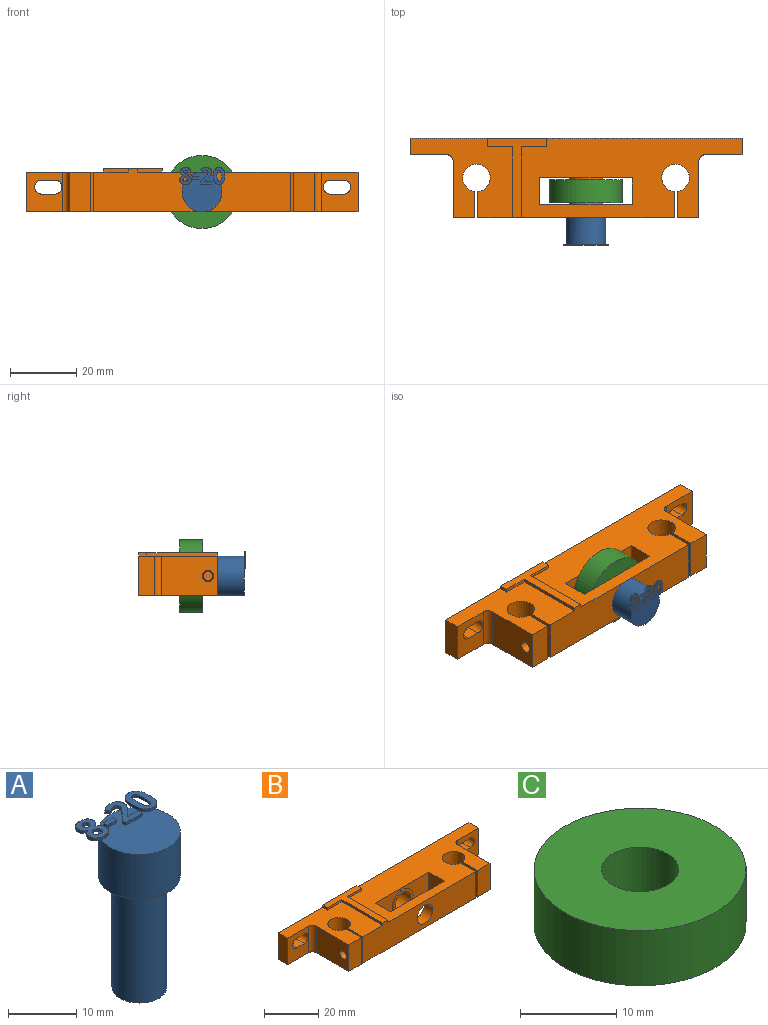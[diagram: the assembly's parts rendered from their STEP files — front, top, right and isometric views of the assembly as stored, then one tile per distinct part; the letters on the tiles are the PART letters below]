
ASSEMBLY  parts=3 mates=2
PART A: 89 faces, bbox 13.6x13.4x28.5 mm
  f0: plane 0.75x0.57mm, normal (0,0,1), area 0.1mm2, adj f5,f78,f79
  f1: plane 12x12mm, normal (0,0,1), area 100.3mm2, adj f5,f22,f23,f24,f25,f26,f40,f41
  f2: plane 1.04x0.97mm, normal (0,0,1), area 0.5mm2, adj f5,f29,f30,f31,f32,f33
  f3: cylinder r=4mm len=20mm, axis (0,0,-1), area 502.7mm2, adj f4,f6
  f4: plane 8x8mm, normal (0,0,-1), area 50.3mm2, adj f3
  f5: cylinder r=6mm len=12mm, axis (0,0,-1), area 301.6mm2, adj f0,f1,f2,f6,f39,f70,f88
  f6: plane 12x12mm, normal (0,0,-1), area 62.8mm2, adj f3,f5
  f7: extruded ~0.5x0.43mm, area 0.2mm2, adj f8,f37,f38,f39
  f8: extruded ~0.5x0.43mm, area 0.2mm2, adj f7,f9,f38,f39
  f9: extruded ~0.5x0.37mm, area 0.2mm2, adj f8,f10,f38,f39
  f10: extruded ~0.5x0.38mm, area 0.2mm2, adj f9,f11,f38,f39
  f11: extruded ~0.5x0.46mm, area 0.3mm2, adj f10,f12,f38,f39
  f12: extruded ~0.5x0.47mm, area 0.3mm2, adj f11,f13,f38,f39
  f13: extruded ~0.5x0.36mm, area 0.2mm2, adj f12,f37,f38,f39
  f14: extruded ~1.15x0.5mm, area 0.6mm2, adj f15,f35,f38,f39
  f15: extruded ~1.15x0.5mm, area 0.6mm2, adj f14,f16,f38,f39
  f16: extruded ~0.86x0.5mm, area 0.5mm2, adj f15,f17,f38,f39
  f17: extruded ~0.67x0.5mm, area 0.4mm2, adj f16,f18,f38,f39
  f18: extruded ~0.61x0.57mm, area 0.4mm2, adj f17,f19,f38,f39
  f19: extruded ~0.72x0.58mm, area 0.5mm2, adj f18,f20,f38,f39
  f20: extruded ~0.75x0.5mm, area 0.4mm2, adj f19,f21,f38,f39
  f21: extruded ~0.98x0.5mm, area 0.6mm2, adj f20,f22,f38,f39
  f22: extruded ~1.28x0.5mm, area 0.7mm2, adj f1,f21,f23,f38,f39
  f23: extruded ~1.26x0.5mm, area 0.7mm2, adj f1,f22,f24,f38
  f24: extruded ~0.98x0.5mm, area 0.6mm2, adj f1,f23,f25,f38
  f25: extruded ~0.71x0.5mm, area 0.4mm2, adj f1,f24,f26,f38
  f26: extruded ~0.8x0.62mm, area 0.5mm2, adj f1,f25,f27,f38,f39
  f27: extruded ~0.68x0.53mm, area 0.4mm2, adj f26,f28,f38,f39
  f28: extruded ~0.68x0.5mm, area 0.4mm2, adj f27,f35,f38,f39
  f29: extruded ~0.62x0.5mm, area 0.4mm2, adj f2,f30,f36,f38,f39
  f30: extruded ~0.5x0.43mm, area 0.2mm2, adj f2,f29,f31,f38
  f31: extruded ~0.5x0.44mm, area 0.2mm2, adj f2,f30,f32,f38
  f32: extruded ~0.58x0.5mm, area 0.3mm2, adj f2,f31,f33,f38
  f33: extruded ~0.56x0.5mm, area 0.3mm2, adj f2,f32,f34,f38,f39
  f34: extruded ~0.5x0.45mm, area 0.3mm2, adj f33,f36,f38,f39
  f35: extruded ~0.87x0.5mm, area 0.5mm2, adj f14,f28,f38,f39
  f36: extruded ~0.84x0.72mm, area 0.6mm2, adj f29,f34,f38,f39
  f37: extruded ~0.5x0.37mm, area 0.2mm2, adj f7,f13,f38,f39
  f38: plane 5.09x3.48mm, normal (0,0,1), area 11.2mm2, adj f7,f8,f9,f10,f11,f12,f13,f14
  f39: plane 5.05x3.32mm, normal (0,0,-1), area 8.6mm2, adj f5,f7,f8,f9,f10,f11,f12,f13
  f40: plane 0.85x0.5mm, normal (-1,0,0), area 0.4mm2, adj f1,f41,f43,f44
  f41: plane 1.82x0.5mm, normal (0,-1,0), area 0.9mm2, adj f1,f40,f42,f44
  f42: plane 0.85x0.5mm, normal (1,0,0), area 0.4mm2, adj f1,f41,f43,f44
  f43: plane 1.82x0.5mm, normal (0,1,0), area 0.9mm2, adj f1,f40,f42,f44
  f44: plane 1.82x0.85mm, normal (0,0,1), area 1.5mm2, adj f40,f41,f42,f43
  f45: extruded ~0.5x0.39mm, area 0.2mm2, adj f1,f46,f68,f69,f70
  f46: extruded ~0.5x0.41mm, area 0.2mm2, adj f1,f45,f47,f69
  f47: extruded ~0.78x0.72mm, area 0.5mm2, adj f1,f46,f48,f69
  f48: plane 1.26x1.24mm, normal (-0.71,0.7,0), area 0.9mm2, adj f1,f47,f49,f69
  f49: plane 0.73x0.5mm, normal (-1,0,0), area 0.4mm2, adj f1,f48,f50,f69
  f50: plane 3.46x0.5mm, normal (0,-1,0), area 1.7mm2, adj f1,f49,f51,f69
  f51: plane 0.88x0.5mm, normal (1,0,0), area 0.4mm2, adj f1,f50,f52,f69
  f52: plane 2.16x0.5mm, normal (0,1,0), area 1.1mm2, adj f1,f51,f53,f69
  f53: plane 0.5x0.05mm, normal (1,0,0), area 0mm2, adj f1,f52,f54,f69
  f54: plane 0.64x0.6mm, normal (0.69,-0.73,0), area 0.4mm2, adj f1,f53,f55,f69
  f55: extruded ~0.9x0.89mm, area 0.6mm2, adj f1,f54,f56,f69
  f56: extruded ~0.62x0.5mm, area 0.4mm2, adj f1,f55,f57,f69,f70
  f57: extruded ~0.64x0.5mm, area 0.3mm2, adj f56,f58,f69,f70
  f58: extruded ~0.7x0.5mm, area 0.4mm2, adj f57,f59,f69,f70
  f59: extruded ~0.55x0.5mm, area 0.4mm2, adj f58,f60,f69,f70
  f60: extruded ~0.82x0.5mm, area 0.4mm2, adj f59,f61,f69,f70
  f61: extruded ~0.64x0.5mm, area 0.3mm2, adj f60,f62,f69,f70
  f62: extruded ~0.53x0.5mm, area 0.3mm2, adj f61,f63,f69,f70
  f63: extruded ~0.61x0.5mm, area 0.4mm2, adj f62,f64,f69,f70
  f64: plane 0.67x0.57mm, normal (-0.76,-0.65,0), area 0.4mm2, adj f63,f65,f69,f70
  f65: extruded ~0.57x0.5mm, area 0.3mm2, adj f64,f66,f69,f70
  f66: extruded ~0.56x0.5mm, area 0.3mm2, adj f65,f67,f69,f70
  f67: extruded ~0.5x0.44mm, area 0.2mm2, adj f66,f68,f69,f70
  f68: extruded ~0.5x0.44mm, area 0.2mm2, adj f45,f67,f69,f70
  f69: plane 5.03x3.48mm, normal (0,0,1), area 9.1mm2, adj f45,f46,f47,f48,f49,f50,f51,f52
  f70: plane 3.34x2.04mm, normal (0,0,-1), area 3.5mm2, adj f5,f45,f56,f57,f58,f59,f60,f61
  f71: extruded ~1.92x0.5mm, area 1mm2, adj f72,f86,f87,f88
  f72: extruded ~1.91x0.5mm, area 1mm2, adj f71,f73,f87,f88
  f73: extruded ~1.3x0.65mm, area 0.8mm2, adj f72,f74,f87,f88
  f74: extruded ~1.3x0.62mm, area 0.8mm2, adj f73,f75,f87,f88
  f75: extruded ~1.93x0.5mm, area 1mm2, adj f1,f74,f76,f87,f88
  f76: extruded ~1.9x0.5mm, area 1mm2, adj f1,f75,f77,f87
  f77: extruded ~1.29x0.64mm, area 0.8mm2, adj f1,f76,f86,f87
  f78: extruded ~0.53x0.5mm, area 0.4mm2, adj f0,f79,f85,f87,f88
  f79: extruded ~1.31x0.5mm, area 0.7mm2, adj f0,f78,f80,f87,f88
  f80: extruded ~1.31x0.5mm, area 0.7mm2, adj f79,f81,f87,f88
  f81: extruded ~0.53x0.5mm, area 0.4mm2, adj f80,f82,f87,f88
  f82: extruded ~0.53x0.5mm, area 0.4mm2, adj f81,f83,f87,f88
  f83: extruded ~1.31x0.5mm, area 0.7mm2, adj f82,f84,f87,f88
  f84: extruded ~1.3x0.5mm, area 0.7mm2, adj f83,f85,f87,f88
  f85: extruded ~0.53x0.5mm, area 0.4mm2, adj f78,f84,f87,f88
  f86: extruded ~1.31x0.62mm, area 0.8mm2, adj f1,f71,f77,f87,f88
  f87: plane 5.1x3.46mm, normal (0,0,1), area 10.7mm2, adj f71,f72,f73,f74,f75,f76,f77,f78
  f88: plane 5.1x3.46mm, normal (0,0,-1), area 8.4mm2, adj f5,f71,f72,f73,f74,f75,f78,f79
PART B: 53 faces, bbox 100x24x13 mm
  f0: plane 100x24mm, normal (0,0,1), area 1458.9mm2, adj f2,f3,f4,f5,f6,f7,f8,f9
  f1: plane 100x24mm, normal (0,0,-1), area 1561.7mm2, adj f2,f3,f4,f5,f6,f7,f8,f9
  f2: plane 100x12mm, normal (0,1,0), area 1138.7mm2, adj f0,f1,f6,f11,f18,f19,f20,f21
  f3: plane 12x11mm, normal (0,-1,0), area 101.3mm2, adj f0,f1,f11,f22,f23,f24,f25,f48
  f4: plane 12x6.56mm, normal (0,-1,0), area 78.7mm2, adj f0,f1,f10,f16
  f5: plane 59.12x13mm, normal (0,-1,0), area 659.4mm2, adj f0,f1,f14,f17,f26,f37,f38,f44
  f6: plane 12x5mm, normal (-1,0,0), area 60mm2, adj f0,f1,f2,f7
  f7: plane 12x11mm, normal (0,-1,0), area 101.3mm2, adj f0,f1,f6,f18,f19,f20,f21,f52
  f8: plane 17x12mm, normal (-1,0,0), area 194.9mm2, adj f0,f1,f9,f51,f52
  f9: plane 12x6.56mm, normal (0,-1,0), area 78.7mm2, adj f0,f1,f8,f13
  f10: plane 17x12mm, normal (1,0,0), area 194.9mm2, adj f0,f1,f4,f47,f48
  f11: plane 12x5mm, normal (1,0,0), area 60mm2, adj f0,f1,f2,f3
  f12: cylinder r=4.15mm len=12mm, axis (0,0,1), area 302.4mm2, adj f0,f1,f13,f14
  f13: plane 12x7.87mm, normal (1,0,0), area 85.4mm2, adj f0,f1,f9,f12,f51
  f14: plane 12x7.87mm, normal (-1,0,0), area 88.3mm2, adj f0,f1,f5,f12,f50
  f15: cylinder r=4.15mm len=12mm, axis (0,0,1), area 302.4mm2, adj f0,f1,f16,f17
  f16: plane 12x7.87mm, normal (-1,0,0), area 85.4mm2, adj f0,f1,f4,f15,f47
  f17: plane 12x7.87mm, normal (1,0,0), area 88.3mm2, adj f0,f1,f5,f15,f46
  f18: cylinder r=2.1mm len=5mm, axis (0,1,0), area 33mm2, adj f2,f7,f19,f21
  f19: plane 5x4mm, normal (0,0,1), area 20mm2, adj f2,f7,f18,f20
  f20: cylinder r=2.1mm len=5mm, axis (0,1,0), area 33mm2, adj f2,f7,f19,f21
  f21: plane 5x4mm, normal (0,0,-1), area 20mm2, adj f2,f7,f18,f20
  f22: plane 5x4mm, normal (0,0,-1), area 20mm2, adj f2,f3,f23,f25
  f23: cylinder r=2.1mm len=5mm, axis (0,1,0), area 33mm2, adj f2,f3,f22,f24
  f24: plane 5x4mm, normal (0,0,1), area 20mm2, adj f2,f3,f23,f25
  f25: cylinder r=2.1mm len=5mm, axis (0,1,0), area 33mm2, adj f2,f3,f22,f24
  f26: cylinder r=4.1mm len=8.2mm, axis (0,-1,0), area 115.9mm2, adj f5,f36
  f27: plane 12x8mm, normal (1,0,0), area 96mm2, adj f0,f1,f29,f30
  f28: plane 12x8mm, normal (-1,0,0), area 96mm2, adj f0,f1,f29,f30
  f29: plane 28x12mm, normal (0,-1,0), area 251.2mm2, adj f0,f1,f27,f28,f31
  f30: plane 28x12mm, normal (0,1,0), area 249.3mm2, adj f0,f1,f27,f28,f35
  f31: cylinder r=5.2mm len=10.39mm, axis (0,1,0), area 16.3mm2, adj f29,f32
  f32: plane 10.39x10.39mm, normal (0,-1,0), area 32mm2, adj f31,f34
  f33: plane 8.2x8.2mm, normal (0,-1,0), area 52.8mm2, adj f34
  f34: cylinder r=4.1mm len=8.5mm, axis (0,-1,0), area 219mm2, adj f32,f33
  f35: cylinder r=5.25mm len=10.51mm, axis (0,-1,0), area 16.5mm2, adj f30,f36
  f36: plane 10.51x10.51mm, normal (0,1,0), area 33.9mm2, adj f26,f35
  f37: plane 21.34x1mm, normal (-1,0,0), area 21.3mm2, adj f0,f5,f43,f44
  f38: plane 21.34x1mm, normal (1,0,0), area 21.3mm2, adj f0,f5,f39,f44
  f39: plane 7.54x1mm, normal (0,-1,0), area 7.5mm2, adj f0,f38,f40,f44
  f40: plane 2.46x1mm, normal (1,0,0), area 2.5mm2, adj f0,f39,f41,f44
  f41: plane 17.84x1mm, normal (0,1,0), area 17.8mm2, adj f0,f40,f42,f44
  f42: plane 2.46x1mm, normal (-1,0,0), area 2.5mm2, adj f0,f41,f43,f44
  f43: plane 7.54x1mm, normal (0,-1,0), area 7.5mm2, adj f0,f37,f42,f44
  f44: plane 23.8x17.84mm, normal (0,0,1), area 102.9mm2, adj f5,f37,f38,f39,f40,f41,f42,f43
  f45: plane 2.8x2.8mm, normal (1,0,0), area 6.2mm2, adj f46
  f46: cylinder r=1.4mm len=10.56mm, axis (1,0,0), area 92.9mm2, adj f17,f45
  f47: cylinder r=1.7mm len=6.56mm, axis (1,0,0), area 70.1mm2, adj f10,f16
  f48: cylinder r=2mm len=12mm, axis (0,0,1), area 37.7mm2, adj f0,f1,f3,f10
  f49: plane 2.8x2.8mm, normal (-1,0,0), area 6.2mm2, adj f50
  f50: cylinder r=1.4mm len=10.56mm, axis (-1,0,0), area 92.9mm2, adj f14,f49
  f51: cylinder r=1.7mm len=6.56mm, axis (-1,0,0), area 70.1mm2, adj f8,f13
  f52: cylinder r=2mm len=12mm, axis (0,0,1), area 37.7mm2, adj f0,f1,f7,f8
PART C: 4 faces, bbox 22x22x7 mm
  f0: cylinder r=4mm len=8mm, axis (0,0,-1), area 175.9mm2, adj f2,f3
  f1: cylinder r=11mm len=22mm, axis (0,0,-1), area 483.8mm2, adj f2,f3
  f2: plane 22x22mm, normal (0,0,1), area 329.9mm2, adj f0,f1
  f3: plane 22x22mm, normal (0,0,-1), area 329.9mm2, adj f0,f1
PLACE A rot(axis=(1,0,0),90deg) t=(5.95,13.74,6.05)mm
PLACE B t=(-0.7,5.43,0.05)mm
PLACE C rot(axis=(-1,0,0),90deg) t=(5.95,-1.76,6.05)mm
MATE fastened C.f0 <-> B.f26  axis (0,1,0) through (5.95,5.24,6.05)mm
MATE fastened A.f3 <-> B.f26  axis (0,1,0) through (5.95,-6.26,6.05)mm
